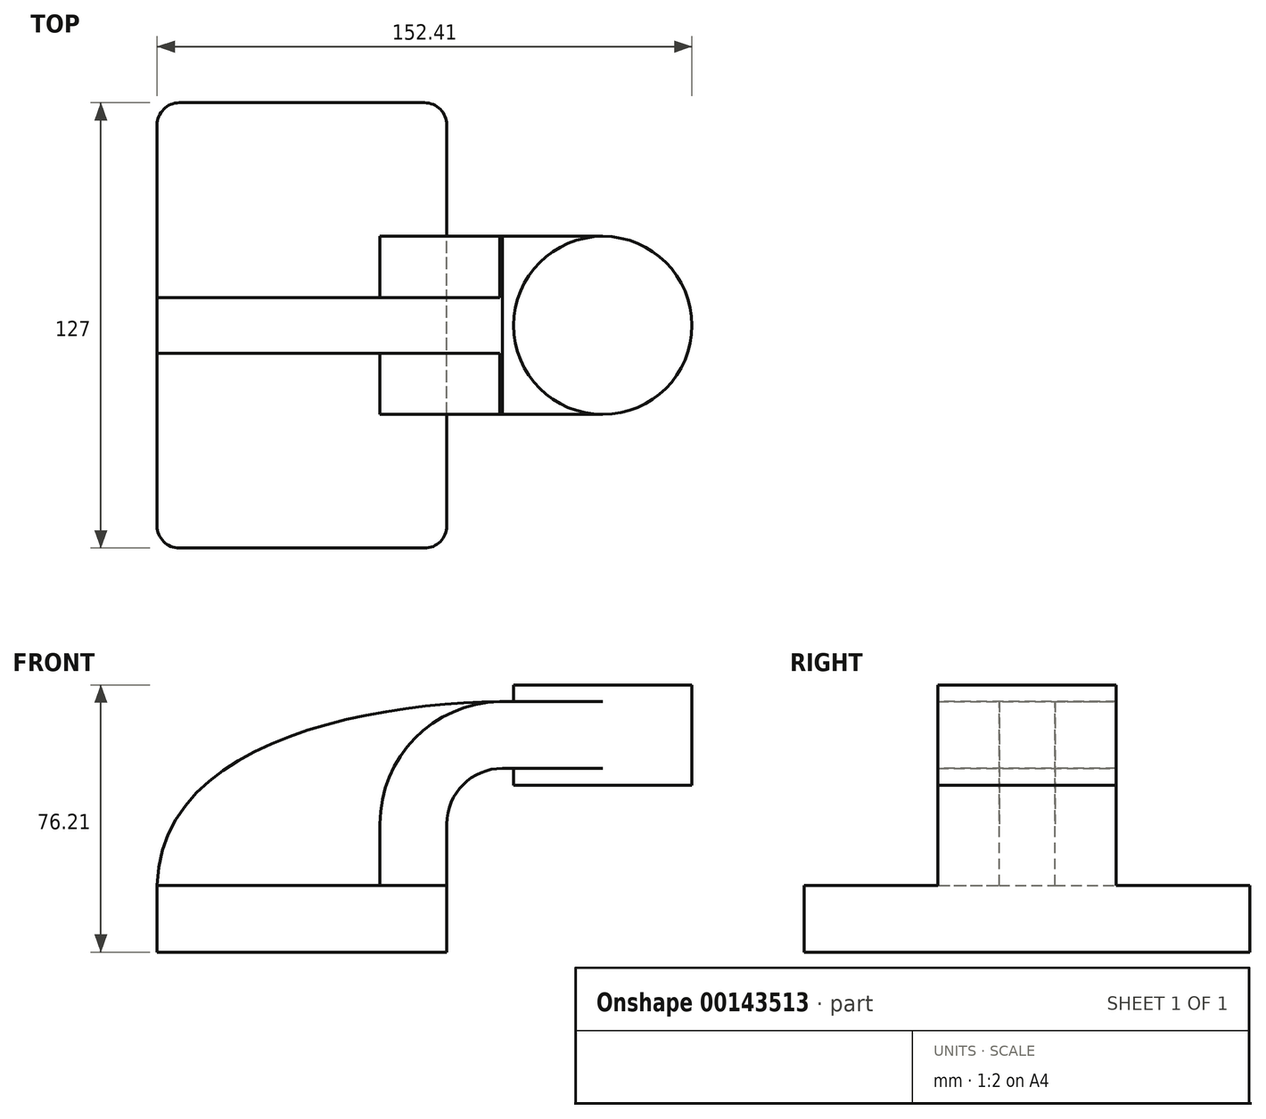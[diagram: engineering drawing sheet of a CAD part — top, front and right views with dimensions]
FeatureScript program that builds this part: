
annotation { "Feature Type Name" : "Feature", "Feature Type Description" : "" }
export const myFeature = defineFeature(function(context is Context, id is Id, definition is map)
    precondition{}
    {
        {
            var Q0;
            Q0=qCreatedBy(makeId("Front.planeOp"),FACE);
            var sketch = newSketch(context, id + "F0", { "sketchPlane" : qUnion([Q0])});
            skLineSegment(sketch, "E0.bottom", {"start": v(41.28, -9.52) * mm, "end": v(-41.28, -9.53) * mm});
            skLineSegment(sketch, "E0.top", {"start": v(41.28, 9.53) * mm, "end": v(-41.28, 9.53) * mm});
            skLineSegment(sketch, "E0.left", {"start": v(41.28, -9.52) * mm, "end": v(41.28, 9.53) * mm});
            skLineSegment(sketch, "E0.right", {"start": v(-41.28, -9.53) * mm, "end": v(-41.28, 9.53) * mm});
            skPoint(sketch, "E0.middle", {"position": v(0, 0) * mm});
            skLineSegment(sketch, "E1.bottom", {"start": v(111.12, 38.1) * mm, "end": v(60.32, 38.1) * mm});
            skLineSegment(sketch, "E1.top", {"start": v(111.12, 66.68) * mm, "end": v(60.32, 66.68) * mm});
            skLineSegment(sketch, "E1.left", {"start": v(111.12, 38.1) * mm, "end": v(111.12, 66.68) * mm});
            skLineSegment(sketch, "E1.right", {"start": v(60.32, 38.1) * mm, "end": v(60.32, 66.68) * mm});
            skPoint(sketch, "E1.middle", {"position": v(85.72, 52.39) * mm});
            skLineSegment(sketch, "E2", {"start": v(41.28, 9.53) * mm, "end": v(41.28, 27) * mm});
            skArc(sketch, "E3", {"start": v(41.27, 27) * mm, "mid": v(45.92, 38.23) * mm, "end": v(57.15, 42.88) * mm});
            skLineSegment(sketch, "E4", {"start": v(57.15, 42.88) * mm, "end": v(85.72, 42.88) * mm});
            skLineSegment(sketch, "E5.0", {"start": v(57.15, 61.93) * mm, "end": v(85.72, 61.93) * mm});
            skArc(sketch, "E5.1", {"start": v(22.23, 27) * mm, "mid": v(32.45, 51.7) * mm, "end": v(57.15, 61.93) * mm});
            skLineSegment(sketch, "E5.2", {"start": v(22.22, 9.53) * mm, "end": v(22.22, 27) * mm});
            skFitSpline(sketch, "E6", {"points": [v(-41.28, 9.52) * mm, v(57.15, 61.93) * mm], "startDerivative": vector(2.76, 124.16) * mm, "endDerivative": vector(112.28, 1.14) * mm});
            skLineSegment(sketch, "E7", {"start": v(85.72, 66.68) * mm, "end": v(85.72, 38.1) * mm});
            skSolve(sketch);
        }
        {
            var Q0;
            Q0=makeQuery(id+"F0.imprint","IMPRINT",FACE,{"disambiguationData":[TD([[makeQuery(id+"F0.imprint","IMPRINT",EDGE,{"derivedFrom":sQuery(id+"F0.wireOp",EDGE,"E0.bottom")}),-1.0]])]});
            extrude(context, id + "F1", {"entities" : qUnion([Q0]), "endBound" : BoundingType.SYMMETRIC, "depth" : 127 * mm});
        }
        {
            var Q0;
            {var subQ1=sQuery(id+"F0.wireOp",EDGE,"E2");Q0=makeQuery(id+"F0.imprint","IMPRINT",FACE,{"disambiguationData":[TD([[makeQuery(id+"F0.imprint","IMPRINT",EDGE,{"derivedFrom":subQ1}),1.0]])]});}
            var Q1;
            {var subQ5=sQuery(id+"F0.wireOp",EDGE,"DBKJasSQ-kUdJ-3Vua-lQ6w-DGNIqPXDKVXN");Q1=makeQuery(id+"F0.imprint","IMPRINT",FACE,{"disambiguationData":[TD([[makeQuery(id+"F0.imprint","IMPRINT",EDGE,{"derivedFrom":subQ5}),1.0]])]});}
            var Q2;
            {var subQ0=sQuery(id+"F0.wireOp",EDGE,"E4");var subQ1=sQuery(id+"F0.wireOp",EDGE,"E1.right");var subQ2=makeQuery(id+"F0.imprint","INTERSECT",VERTEX,{"derivedFrom":[subQ1,subQ0]});Q2=makeQuery(id+"F0.imprint","IMPRINT",FACE,{"disambiguationData":[TD([[makeQuery(id+"F0.imprint","IMPRINT",EDGE,{"disambiguationData":[TD([[subQ2,-1.0]])],"derivedFrom":subQ1}),-1.0]])]});}
            extrude(context, id + "F2", {"entities" : qUnion([Q0, Q1, Q2]), "operationType" : NewBodyOperationType.ADD, "endBound" : BoundingType.SYMMETRIC, "depth" : 50.8 * mm});
        }
        {
            var Q0;
            {var subQ3=sQuery(id+"F0.wireOp",EDGE,"E5.2");Q0=makeQuery(id+"F0.imprint","IMPRINT",FACE,{"disambiguationData":[TD([[makeQuery(id+"F0.imprint","IMPRINT",EDGE,{"derivedFrom":subQ3}),1.0]])]});}
            extrude(context, id + "F3", {"entities" : qUnion([Q0]), "operationType" : NewBodyOperationType.ADD, "endBound" : BoundingType.SYMMETRIC, "depth" : 15.88 * mm});
        }
        {
            var Q0;
            {var subQ4=sQuery(id+"F0.wireOp",EDGE,"E1.left");Q0=makeQuery(id+"F0.imprint","IMPRINT",FACE,{"disambiguationData":[TD([[makeQuery(id+"F0.imprint","IMPRINT",EDGE,{"derivedFrom":subQ4}),1.0]])]});}
            var Q1;
            Q1=sQuery(id+"F0.wireOp",EDGE,"E7");
            revolve(context, id + "F4", {"operationType" : NewBodyOperationType.ADD, "entities" : qUnion([Q0]), "axis" : qUnion([Q1]), "revolveType" : RevolveType.FULL});
        }
        {
            var Q0;
            Q0=makeQuery(id+"F1.opExtrude","CAP_EDGE",EDGE,{"disambiguationData":[OSD([sQuery(id+"F0.wireOp",EDGE,"E0.right")])],"isStart":false});
            var Q1;
            Q1=makeQuery(id+"F1.opExtrude","CAP_EDGE",EDGE,{"disambiguationData":[OSD([sQuery(id+"F0.wireOp",EDGE,"E0.left")])],"isStart":false});
            var Q2;
            Q2=makeQuery(id+"F1.opExtrude","CAP_EDGE",EDGE,{"disambiguationData":[OSD([sQuery(id+"F0.wireOp",EDGE,"E0.left")])],"isStart":true});
            var Q3;
            Q3=makeQuery(id+"F1.opExtrude","CAP_EDGE",EDGE,{"disambiguationData":[OSD([sQuery(id+"F0.wireOp",EDGE,"E0.right")])],"isStart":true});
            fillet(context, id + "F5", {"entities" : qUnion([Q0, Q1, Q2, Q3]), "radius" : 6.35 * mm, "tangentPropagation" : true, "allowEdgeOverflow" : false});
        }
    });
